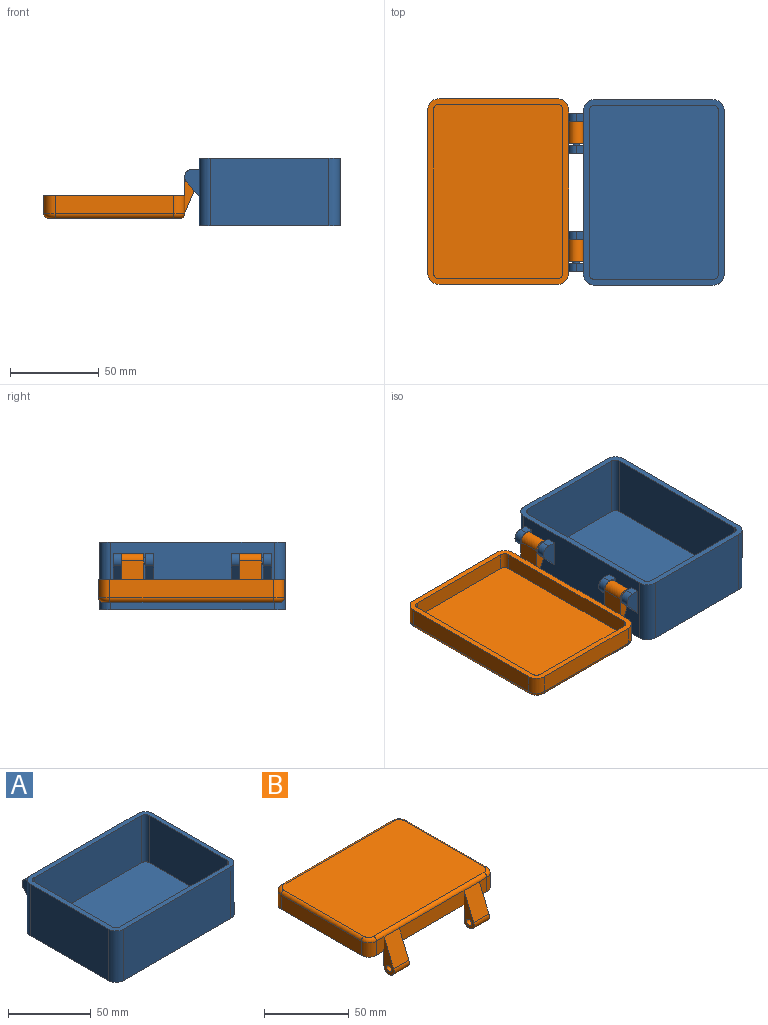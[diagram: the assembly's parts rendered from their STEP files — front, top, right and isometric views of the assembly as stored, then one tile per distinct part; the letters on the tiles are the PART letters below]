
ASSEMBLY  parts=2 mates=1
PART A: 41 faces, bbox 104.8x87.8x38.1 mm
  f0: plane 92.08x38.1mm, normal (0,1,0), area 3213.9mm2, adj f1,f2,f4,f8,f9,f12,f23,f24
  f1: plane 4.83x4.16mm, normal (0,0,1), area 20.1mm2, adj f0,f22,f25,f28
  f2: plane 8.23x7.32mm, normal (0,0.75,-0.66), area 53.2mm2, adj f0,f3,f26,f27
  f3: cylinder r=4.21mm len=7.01mm, axis (-1,0,0), area 46.8mm2, adj f2,f23,f26,f27
  f4: plane 104.78x79.38mm, normal (0,0,1), area 1103.1mm2, adj f0,f5,f6,f7,f9,f10,f11,f12
  f5: plane 66.68x38.1mm, normal (-1,0,0), area 2540.3mm2, adj f4,f8,f9,f10
  f6: plane 92.08x38.1mm, normal (0,-1,0), area 3508.1mm2, adj f4,f8,f10,f11
  f7: plane 66.68x38.1mm, normal (1,0,0), area 2540.3mm2, adj f4,f8,f11,f12
  f8: plane 104.78x79.38mm, normal (0,0,-1), area 8281.9mm2, adj f0,f5,f6,f7,f9,f10,f11,f12
  f9: cylinder r=6.35mm len=38.1mm, axis (0,0,-1), area 380mm2, adj f0,f4,f5,f8
  f10: cylinder r=6.35mm len=38.1mm, axis (0,0,1), area 380mm2, adj f4,f5,f6,f8
  f11: cylinder r=6.35mm len=38.1mm, axis (0,0,-1), area 380mm2, adj f4,f6,f7,f8
  f12: cylinder r=6.35mm len=38.1mm, axis (0,0,1), area 380mm2, adj f0,f4,f7,f8
  f13: plane 92.08x34.93mm, normal (0,-1,0), area 3215.7mm2, adj f4,f17,f18,f21
  f14: plane 66.68x34.93mm, normal (1,0,0), area 2328.6mm2, adj f4,f17,f18,f19
  f15: plane 92.08x34.93mm, normal (0,1,0), area 3215.7mm2, adj f4,f17,f19,f20
  f16: plane 66.68x34.93mm, normal (-1,0,0), area 2328.6mm2, adj f4,f17,f20,f21
  f17: plane 98.43x73.03mm, normal (0,0,1), area 7178.8mm2, adj f13,f14,f15,f16,f18,f19,f20,f21
  f18: cylinder r=3.17mm len=34.93mm, axis (0,0,-1), area 174.2mm2, adj f4,f13,f14,f17
  f19: cylinder r=3.17mm len=34.93mm, axis (0,0,1), area 174.2mm2, adj f4,f14,f15,f17
  f20: cylinder r=3.17mm len=34.93mm, axis (0,0,-1), area 174.2mm2, adj f4,f15,f16,f17
  f21: cylinder r=3.17mm len=34.93mm, axis (0,0,1), area 174.2mm2, adj f4,f13,f16,f17
  f22: cylinder r=4.21mm len=7.01mm, axis (-1,0,0), area 46.8mm2, adj f1,f24,f25,f28
  f23: plane 4.83x4.16mm, normal (0,0,1), area 20.1mm2, adj f0,f3,f26,f27
  f24: plane 8.23x7.32mm, normal (0,0.75,-0.66), area 53.2mm2, adj f0,f22,f25,f28
  f25: plane 15.24x8.39mm, normal (1,0,0), area 84.2mm2, adj f0,f1,f22,f24
  f26: plane 15.24x8.39mm, normal (-1,0,0), area 84.2mm2, adj f0,f2,f3,f23
  f27: plane 15.24x8.39mm, normal (1,0,0), area 71.8mm2, adj f0,f2,f3,f23,f29
  f28: plane 15.24x8.39mm, normal (-1,0,0), area 71.8mm2, adj f0,f1,f22,f24,f29
  f29: cylinder r=1.98mm len=13.21mm, axis (1,0,0), area 164.7mm2, adj f27,f28
  f30: plane 4.83x4.16mm, normal (0,0,1), area 20.1mm2, adj f0,f33,f36,f39
  f31: plane 8.23x7.32mm, normal (0,0.75,-0.66), area 53.2mm2, adj f0,f32,f37,f38
  f32: cylinder r=4.21mm len=7.01mm, axis (1,0,0), area 46.8mm2, adj f31,f34,f37,f38
  f33: cylinder r=4.21mm len=7.01mm, axis (1,0,0), area 46.8mm2, adj f30,f35,f36,f39
  f34: plane 4.83x4.16mm, normal (0,0,1), area 20.1mm2, adj f0,f32,f37,f38
  f35: plane 8.23x7.32mm, normal (0,0.75,-0.66), area 53.2mm2, adj f0,f33,f36,f39
  f36: plane 15.24x8.39mm, normal (-1,0,0), area 84.2mm2, adj f0,f30,f33,f35
  f37: plane 15.24x8.39mm, normal (1,0,0), area 84.2mm2, adj f0,f31,f32,f34
  f38: plane 15.24x8.39mm, normal (-1,0,0), area 71.8mm2, adj f0,f31,f32,f34,f40
  f39: plane 15.24x8.39mm, normal (1,0,0), area 71.8mm2, adj f0,f30,f33,f35,f40
  f40: cylinder r=1.98mm len=13.21mm, axis (-1,0,0), area 164.7mm2, adj f38,f39
PART B: 41 faces, bbox 105.8x88.3x27.5 mm
  f0: plane 10.32x6.35mm, normal (0,-1,0), area 65.5mm2, adj f2,f11,f13,f37
  f1: plane 53.98x10.32mm, normal (0,-1,0), area 557mm2, adj f2,f13,f33,f38
  f2: plane 104.78x79.38mm, normal (0,0,-1), area 1103.1mm2, adj f0,f1,f3,f4,f5,f6,f8,f9
  f3: plane 66.68x10.32mm, normal (1,0,0), area 688mm2, adj f2,f8,f11,f17
  f4: plane 92.08x10.32mm, normal (0,1,0), area 950.1mm2, adj f2,f8,f9,f18
  f5: plane 66.68x10.32mm, normal (-1,0,0), area 688mm2, adj f2,f9,f10,f14
  f6: plane 10.32x6.35mm, normal (0,-1,0), area 65.5mm2, adj f2,f10,f13,f32
  f7: plane 100.01x74.61mm, normal (0,0,1), area 7448.7mm2, adj f12,f13,f14,f15,f16,f17,f18,f19
  f8: cylinder r=6.35mm len=10.32mm, axis (0,0,-1), area 102.9mm2, adj f2,f3,f4,f19
  f9: cylinder r=6.35mm len=10.32mm, axis (0,0,1), area 102.9mm2, adj f2,f4,f5,f16
  f10: cylinder r=6.35mm len=10.32mm, axis (0,0,-1), area 102.9mm2, adj f2,f5,f6,f12
  f11: cylinder r=6.35mm len=10.32mm, axis (0,0,1), area 102.9mm2, adj f0,f2,f3,f15
  f12: torus R=3.97mm, axis (0,0,1), area 32.2mm2, adj f7,f10,f13,f14
  f13: cylinder r=2.38mm len=92.08mm, axis (-1,0,0), area 344.4mm2, adj f0,f1,f6,f7,f12,f15,f29,f34
  f14: cylinder r=2.38mm len=66.68mm, axis (0,1,0), area 249.4mm2, adj f5,f7,f12,f16
  f15: torus R=3.97mm, axis (0,0,1), area 32.2mm2, adj f7,f11,f13,f17
  f16: torus R=3.97mm, axis (0,0,1), area 32.2mm2, adj f7,f9,f14,f18
  f17: cylinder r=2.38mm len=66.68mm, axis (0,-1,0), area 249.4mm2, adj f3,f7,f15,f19
  f18: cylinder r=2.38mm len=92.08mm, axis (1,0,0), area 344.4mm2, adj f4,f7,f16,f19
  f19: torus R=3.97mm, axis (0,0,1), area 32.2mm2, adj f7,f8,f17,f18
  f20: plane 66.68x9.53mm, normal (-1,0,0), area 635.1mm2, adj f2,f24,f25,f28
  f21: plane 92.08x9.53mm, normal (0,-1,0), area 877mm2, adj f2,f24,f25,f26
  f22: plane 66.68x9.53mm, normal (1,0,0), area 635.1mm2, adj f2,f24,f26,f27
  f23: plane 92.08x9.53mm, normal (0,1,0), area 877mm2, adj f2,f24,f27,f28
  f24: plane 98.43x73.03mm, normal (0,0,-1), area 7178.8mm2, adj f20,f21,f22,f23,f25,f26,f27,f28
  f25: cylinder r=3.17mm len=9.53mm, axis (0,0,-1), area 47.5mm2, adj f2,f20,f21,f24
  f26: cylinder r=3.17mm len=9.53mm, axis (0,0,1), area 47.5mm2, adj f2,f21,f22,f24
  f27: cylinder r=3.17mm len=9.53mm, axis (0,0,-1), area 47.5mm2, adj f2,f22,f23,f24
  f28: cylinder r=3.17mm len=9.53mm, axis (0,0,1), area 47.5mm2, adj f2,f20,f23,f24
  f29: plane 19.25x12.7mm, normal (0,-0.92,0.39), area 265.2mm2, adj f13,f31,f32,f33
  f30: plane 12.7x10.57mm, normal (0,1,0), area 134.2mm2, adj f2,f31,f32,f33
  f31: cylinder r=4.22mm len=12.7mm, axis (1,0,0), area 189.6mm2, adj f29,f30,f32,f33
  f32: plane 25.1x8.43mm, normal (-1,0,0), area 104.9mm2, adj f6,f29,f30,f31,f40
  f33: plane 25.1x8.43mm, normal (1,0,0), area 104.9mm2, adj f1,f29,f30,f31,f40
  f34: plane 19.25x12.7mm, normal (0,-0.92,0.39), area 265.2mm2, adj f13,f36,f37,f38
  f35: plane 12.7x10.57mm, normal (0,1,0), area 134.2mm2, adj f2,f36,f37,f38
  f36: cylinder r=4.22mm len=12.7mm, axis (-1,0,0), area 189.6mm2, adj f34,f35,f37,f38
  f37: plane 25.1x8.43mm, normal (1,0,0), area 104.9mm2, adj f0,f34,f35,f36,f39
  f38: plane 25.1x8.43mm, normal (-1,0,0), area 104.9mm2, adj f1,f34,f35,f36,f39
  f39: cylinder r=2.16mm len=12.7mm, axis (-1,0,0), area 172.3mm2, adj f37,f38
  f40: cylinder r=2.16mm len=12.7mm, axis (-1,0,0), area 172.3mm2, adj f32,f33
PLACE A rot(axis=(0,0,1),90deg) t=(0,-52.39,0)mm fixed
PLACE B rot(axis=(0.71,-0.71,0),180deg) t=(-87.77,-51.88,16.97)mm
MATE revolute B.f31 <-> A.f29  axis (0,1,0) through (-43.86,-12.19,27.54)mm
